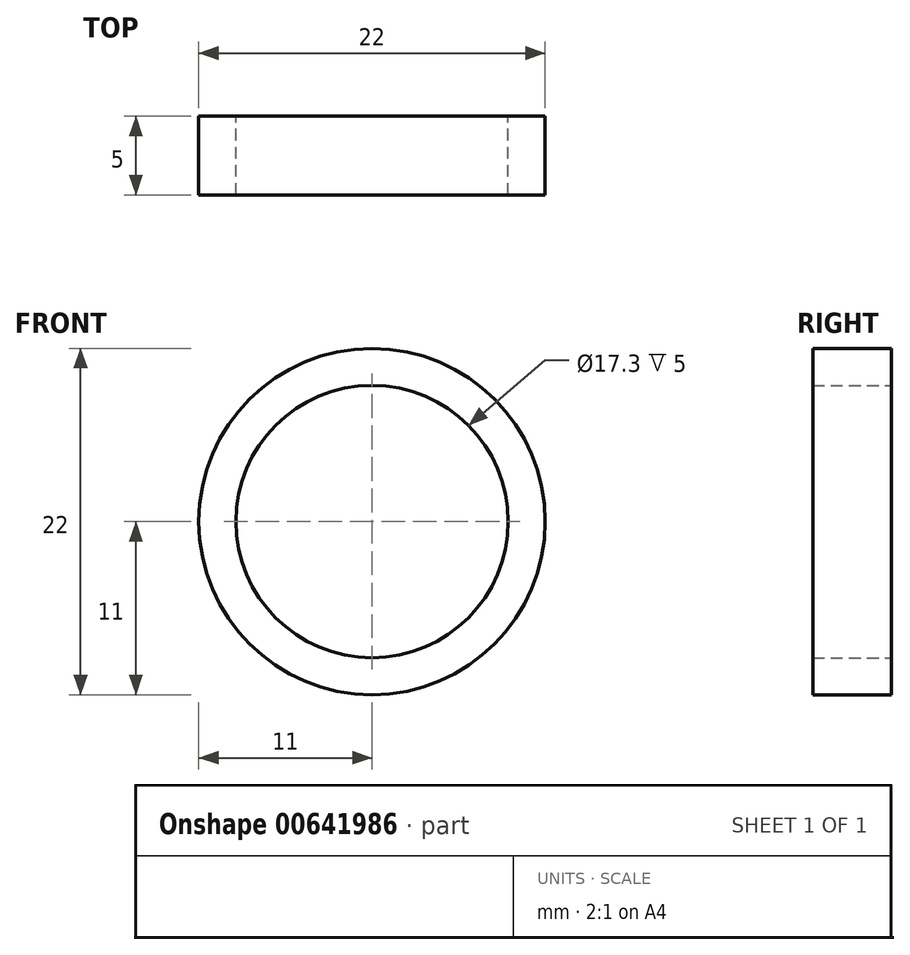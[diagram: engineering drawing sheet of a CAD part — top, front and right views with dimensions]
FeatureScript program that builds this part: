
annotation { "Feature Type Name" : "Feature", "Feature Type Description" : "" }
export const myFeature = defineFeature(function(context is Context, id is Id, definition is map)
    precondition{}
    {
        {
            var Q0;
            Q0=qCreatedBy(makeId("Front.planeOp"),FACE);
            var sketch = newSketch(context, id + "F0", { "sketchPlane" : qUnion([Q0])});
            skCircle(sketch, "E0", {"center": v(0, 0) * mm, "radius": 11 * mm});
            skCircle(sketch, "E1", {"center": v(0, 0) * mm, "radius": 8.65 * mm});
            skSolve(sketch);
        }
        {
            var Q0;
            Q0=makeQuery(id+"F0.imprint","IMPRINT",FACE,{"disambiguationData":[TD([[makeQuery(id+"F0.imprint","IMPRINT",EDGE,{"derivedFrom":sQuery(id+"F0.wireOp",EDGE,"E0")}),1.0]])]});
            extrude(context, id + "F1", {"entities" : qUnion([Q0]), "depth" : 5 * mm, "offsetDistance" : 25 * mm});
        }
    });
